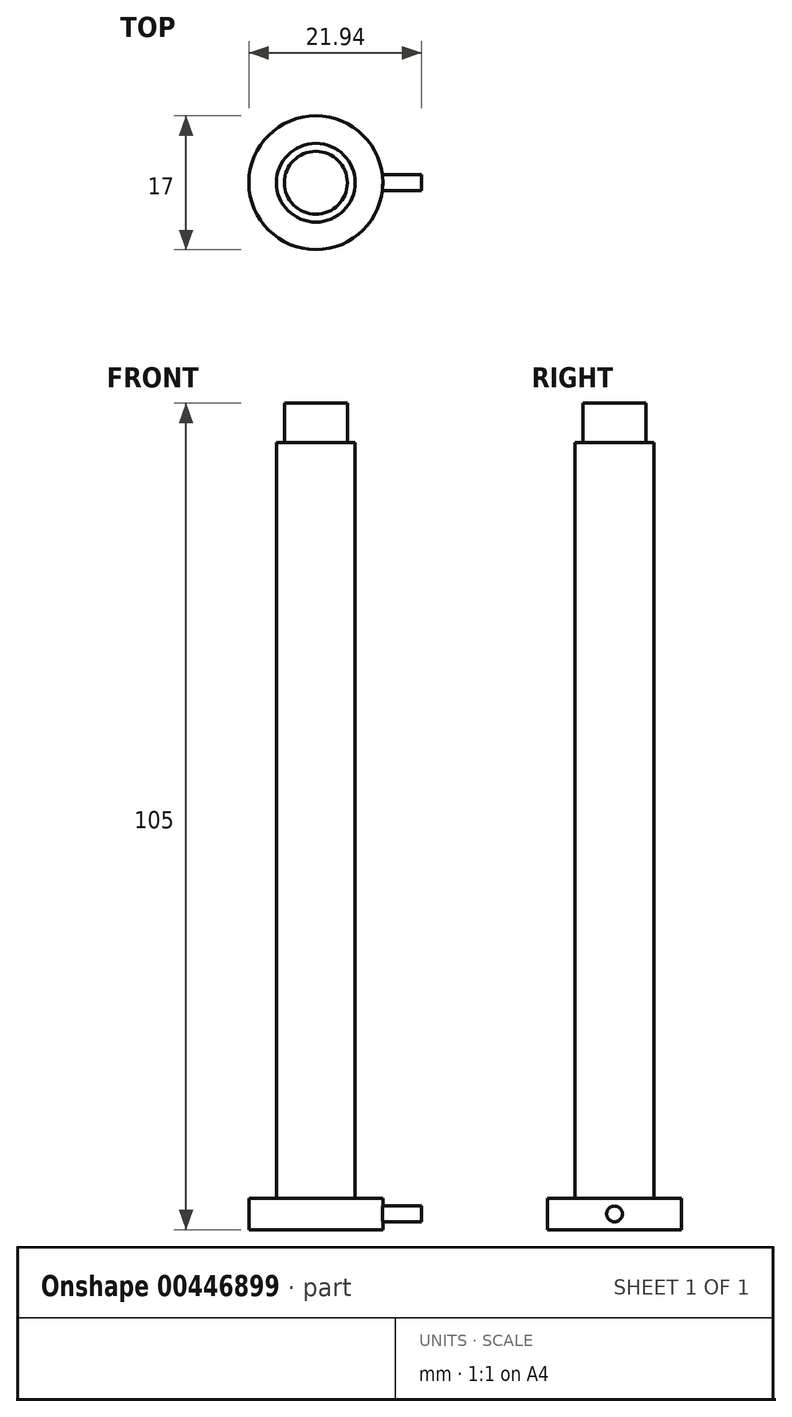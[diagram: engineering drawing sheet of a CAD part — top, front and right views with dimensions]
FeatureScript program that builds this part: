
annotation { "Feature Type Name" : "Feature", "Feature Type Description" : "" }
export const myFeature = defineFeature(function(context is Context, id is Id, definition is map)
    precondition{}
    {
        {
            var Q0;
            Q0=qCreatedBy(makeId("Top.planeOp"),FACE);
            var sketch = newSketch(context, id + "F0", { "sketchPlane" : qUnion([Q0])});
            skCircle(sketch, "E0", {"center": v(0, 0) * mm, "radius": 8.5 * mm});
            skSolve(sketch);
        }
        {
            var Q0;
            Q0=qSketchRegion(id+"F0",true);
            extrude(context, id + "F1", {"entities" : qUnion([Q0]), "depth" : 4 * mm});
        }
        {
            var Q0;
            Q0=qCreatedBy(makeId("Top.planeOp"),FACE);
            cPlane(context, id + "F2", {"entities" : qUnion([Q0]), "cplaneType" : CPlaneType.OFFSET, "offset" : 4 * mm, "width" : 150 * mm, "height" : 150 * mm});
        }
        {
            var Q0;
            Q0=qCreatedBy(makeId("Top.planeOp"),FACE);
            var sketch = newSketch(context, id + "F3", { "sketchPlane" : qUnion([Q0])});
            skCircle(sketch, "E1", {"center": v(0, 0) * mm, "radius": 5 * mm});
            skSolve(sketch);
        }
        {
            var Q0;
            Q0=qSketchRegion(id+"F3",true);
            extrude(context, id + "F4", {"entities" : qUnion([Q0]), "operationType" : NewBodyOperationType.ADD, "depth" : 100 * mm});
        }
        {
            var Q0;
            Q0=qCreatedBy(makeId("Right.planeOp"),FACE);
            var sketch = newSketch(context, id + "F5", { "sketchPlane" : qUnion([Q0])});
            skLineSegment(sketch, "E2.bottom", {"start": v(0, 105) * mm, "end": v(4, 105) * mm});
            skLineSegment(sketch, "E2.top", {"start": v(0, 100) * mm, "end": v(4, 100) * mm});
            skLineSegment(sketch, "E2.left", {"start": v(0, 105) * mm, "end": v(0, 100) * mm});
            skLineSegment(sketch, "E2.right", {"start": v(4, 105) * mm, "end": v(4, 100) * mm});
            skSolve(sketch);
        }
        {
            var Q0;
            Q0=makeQuery(id+"F5.imprint","IMPRINT",FACE,{"disambiguationData":[TD([[makeQuery(id+"F5.imprint","IMPRINT",EDGE,{"derivedFrom":sQuery(id+"F5.wireOp",EDGE,"E2.bottom")}),-1.0]])]});
            var Q1;
            Q1=sQuery(id+"F5.wireOp",EDGE,"E2.left");
            revolve(context, id + "F6", {"operationType" : NewBodyOperationType.ADD, "entities" : qUnion([Q0]), "axis" : qUnion([Q1]), "revolveType" : RevolveType.FULL});
        }
        {
            var Q0;
            Q0=qCreatedBy(id+"F2.planeOp",FACE);
            var sketch = newSketch(context, id + "F7", { "sketchPlane" : qUnion([Q0])});
            skLineSegment(sketch, "E3", {"start": v(8.44, 1) * mm, "end": v(8.44, -1) * mm});
            skSolve(sketch);
        }
        {
            var Q0;
            Q0=sQuery(id+"F7.wireOp",EDGE,"E3");
            cPlane(context, id + "F8", {"entities" : qUnion([Q0]), "cplaneType" : CPlaneType.LINE_ANGLE, "offset" : 25 * mm, "angle" : 90 * degree, "width" : 150 * mm, "height" : 150 * mm});
        }
        {
            var Q0;
            Q0=qCreatedBy(id+"F8.planeOp",FACE);
            var sketch = newSketch(context, id + "F9", { "sketchPlane" : qUnion([Q0])});
            skCircle(sketch, "E4", {"center": v(0, 2) * mm, "radius": 1 * mm});
            skSolve(sketch);
        }
        {
            var Q0;
            Q0=makeQuery(id+"F9.imprint","IMPRINT",FACE,{"disambiguationData":[TD([[makeQuery(id+"F9.imprint","IMPRINT",EDGE,{"derivedFrom":sQuery(id+"F9.wireOp",EDGE,"E4")}),1.0]])]});
            extrude(context, id + "F10", {"entities" : qUnion([Q0]), "operationType" : NewBodyOperationType.ADD, "depth" : 5 * mm});
        }
    });
